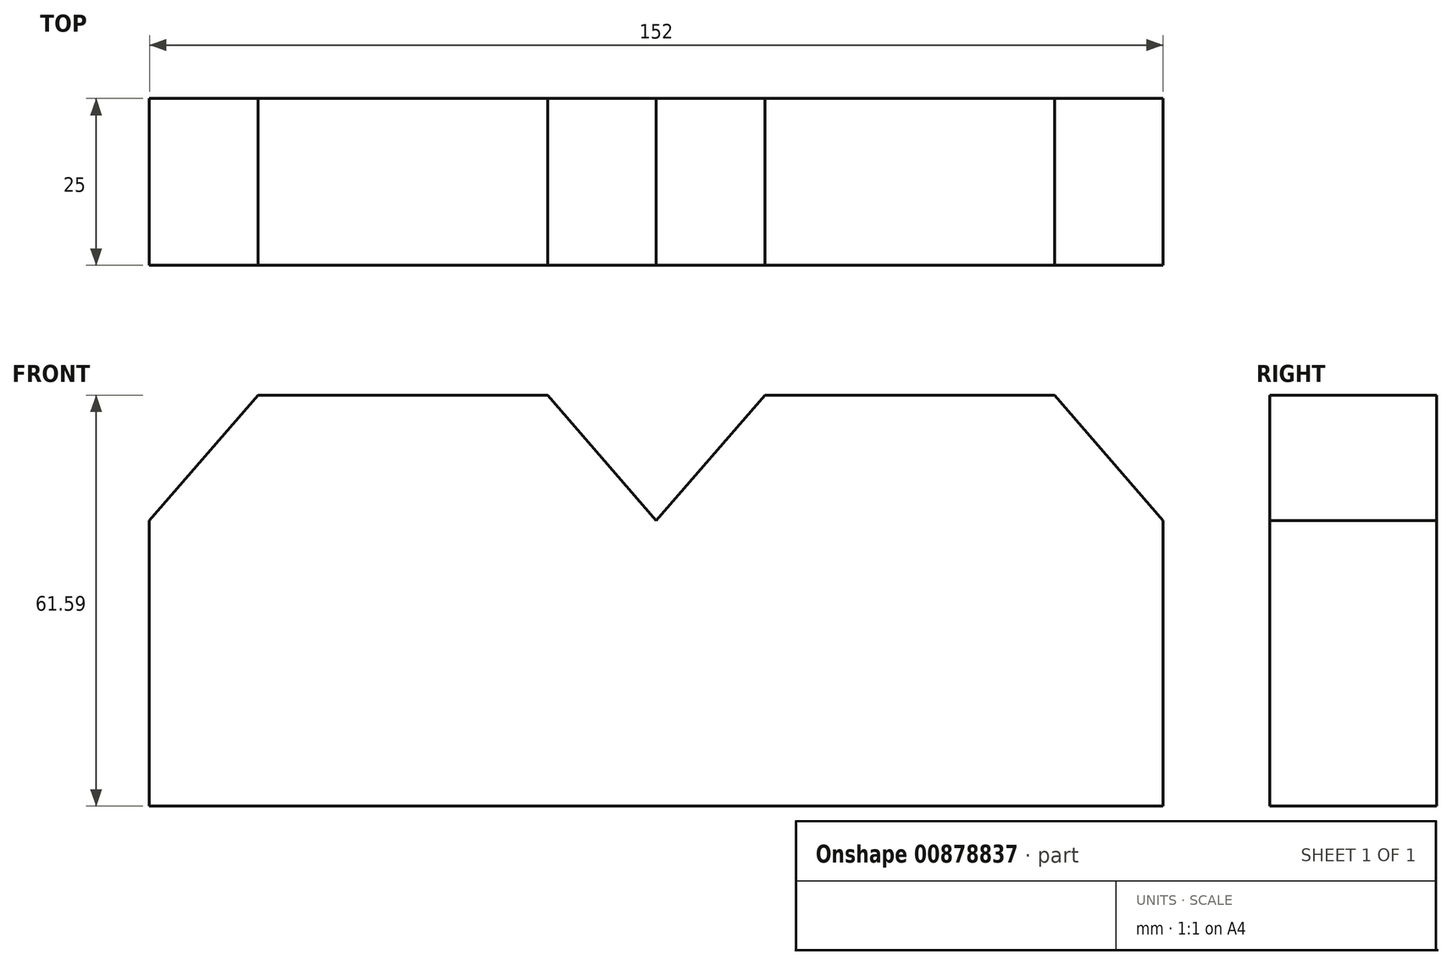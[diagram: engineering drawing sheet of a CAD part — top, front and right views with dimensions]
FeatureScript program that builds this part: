
annotation { "Feature Type Name" : "Feature", "Feature Type Description" : "" }
export const myFeature = defineFeature(function(context is Context, id is Id, definition is map)
    precondition{}
    {
        {
            var Q0;
            Q0=qCreatedBy(makeId("Front.planeOp"),FACE);
            var sketch = newSketch(context, id + "F0", { "sketchPlane" : qUnion([Q0])});
            skLineSegment(sketch, "E0", {"start": v(-142.6, 0) * mm, "end": v(196.05, 0) * mm});
            skLineSegment(sketch, "E1", {"start": v(-97.92, 0) * mm, "end": v(-97.92, 42.8) * mm});
            skLineSegment(sketch, "E2", {"start": v(-97.92, 42.8) * mm, "end": v(-81.64, 61.6) * mm});
            skLineSegment(sketch, "E3", {"start": v(-81.64, 61.6) * mm, "end": v(-59.92, 61.6) * mm});
            skLineSegment(sketch, "E4", {"start": v(-59.92, 83.73) * mm, "end": v(-59.92, -61.6) * mm, "construction": true});
            skLineSegment(sketch, "E5.MirrorCS", {"start": v(-38.2, 61.6) * mm, "end": v(-59.92, 61.6) * mm});
            skLineSegment(sketch, "E6.MirrorCS", {"start": v(-21.92, 42.8) * mm, "end": v(-38.2, 61.6) * mm});
            skLineSegment(sketch, "E7.MirrorCS", {"start": v(-21.92, 0) * mm, "end": v(-21.92, 42.8) * mm});
            skLineSegment(sketch, "E8.1.0.0", {"start": v(-66.6, 0) * mm, "end": v(272.05, 0) * mm});
            skLineSegment(sketch, "E8.1.0.2", {"start": v(-21.92, 42.8) * mm, "end": v(-5.64, 61.6) * mm});
            skLineSegment(sketch, "E8.1.0.3", {"start": v(-5.64, 61.6) * mm, "end": v(16.08, 61.6) * mm});
            skLineSegment(sketch, "E8.1.0.4", {"start": v(37.8, 61.6) * mm, "end": v(16.08, 61.6) * mm});
            skLineSegment(sketch, "E8.1.0.5", {"start": v(54.08, 42.8) * mm, "end": v(37.8, 61.6) * mm});
            skLineSegment(sketch, "E8.1.0.6", {"start": v(54.08, 0) * mm, "end": v(54.08, 42.8) * mm});
            skLineSegment(sketch, "E8.2.0.0", {"start": v(9.4, 0) * mm, "end": v(348.05, 0) * mm});
            skLineSegment(sketch, "E8.2.0.1", {"start": v(54.08, 0) * mm, "end": v(54.08, 42.8) * mm});
            skLineSegment(sketch, "E8.2.0.2", {"start": v(54.08, 42.8) * mm, "end": v(70.36, 61.6) * mm});
            skLineSegment(sketch, "E8.2.0.3", {"start": v(70.36, 61.6) * mm, "end": v(92.08, 61.6) * mm});
            skLineSegment(sketch, "E8.2.0.4", {"start": v(113.8, 61.6) * mm, "end": v(92.08, 61.6) * mm});
            skLineSegment(sketch, "E8.2.0.5", {"start": v(130.08, 42.8) * mm, "end": v(113.8, 61.6) * mm});
            skLineSegment(sketch, "E8.2.0.6", {"start": v(130.08, 0) * mm, "end": v(130.08, 42.8) * mm});
            skLineSegment(sketch, "E8.direction1", {"start": v(-142.6, 0) * mm, "end": v(-66.6, 0) * mm, "construction": true});
            skLineSegment(sketch, "E9", {"start": v(16.08, 85.16) * mm, "end": v(16.08, -53.42) * mm, "construction": true});
            skLineSegment(sketch, "E10", {"start": v(92.08, 81.96) * mm, "end": v(92.08, -55.75) * mm, "construction": true});
            skSolve(sketch);
        }
        {
            var Q0;
            {var subQ0=sQuery(id+"F0.wireOp",EDGE,"E1");Q0=makeQuery(id+"F0.imprint","IMPRINT",FACE,{"disambiguationData":[TD([[makeQuery(id+"F0.imprint","IMPRINT",EDGE,{"derivedFrom":subQ0}),-1.0]])]});}
            var Q1;
            {var subQ0=sQuery(id+"F0.wireOp",EDGE,"E7.MirrorCS");Q1=makeQuery(id+"F0.imprint","IMPRINT",FACE,{"disambiguationData":[TD([[makeQuery(id+"F0.imprint","IMPRINT",EDGE,{"derivedFrom":subQ0}),-1.0]])]});}
            var Q2;
            {var subQ0=sQuery(id+"F0.wireOp",EDGE,"E8.2.0.1");Q2=makeQuery(id+"F0.imprint","IMPRINT",FACE,{"disambiguationData":[TD([[makeQuery(id+"F0.imprint","IMPRINT",EDGE,{"derivedFrom":subQ0}),-1.0]])]});}
            extrude(context, id + "F1", {"entities" : qUnion([Q0, Q1, Q2]), "depth" : 25 * mm, "offsetDistance" : 25 * mm});
        }
    });
